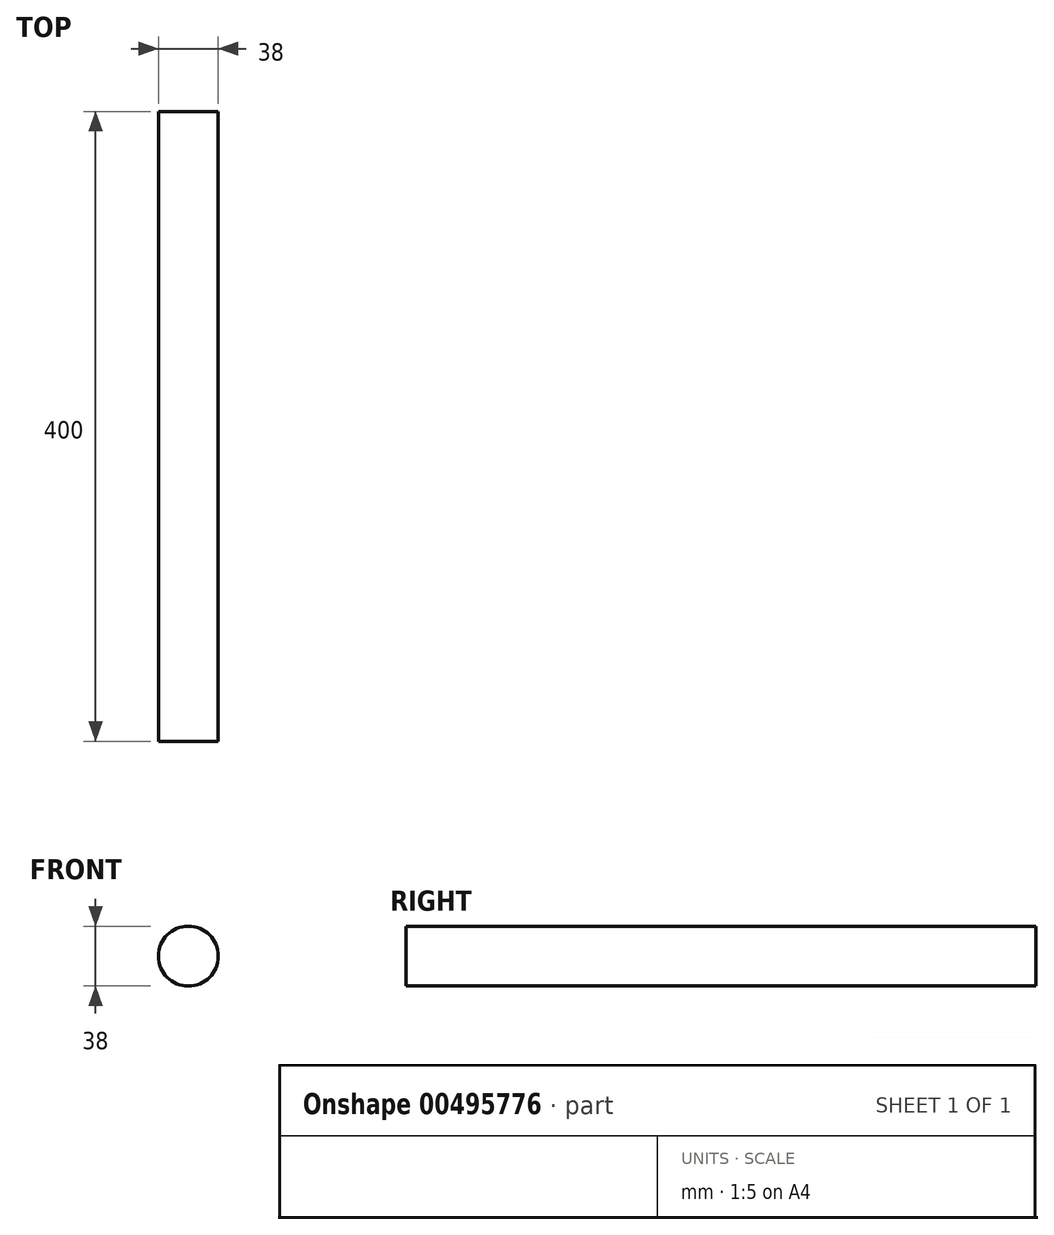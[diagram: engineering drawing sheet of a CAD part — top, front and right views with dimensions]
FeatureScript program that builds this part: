
annotation { "Feature Type Name" : "Feature", "Feature Type Description" : "" }
export const myFeature = defineFeature(function(context is Context, id is Id, definition is map)
    precondition{}
    {
        {
            var Q0;
            Q0=qCreatedBy(makeId("Front.planeOp"),FACE);
            var sketch = newSketch(context, id + "F0", { "sketchPlane" : qUnion([Q0])});
            skCircle(sketch, "E0", {"center": v(-51.25, 40.73) * mm, "radius": 19 * mm});
            skSolve(sketch);
        }
        {
            var Q0;
            Q0 = qSketchRegion(id + "F0", true);
            extrude(context, id + "F1", {"entities" : qUnion([Q0]), "endBound" : BoundingType.SYMMETRIC, "depth" : 400 * mm});
        }
    });
